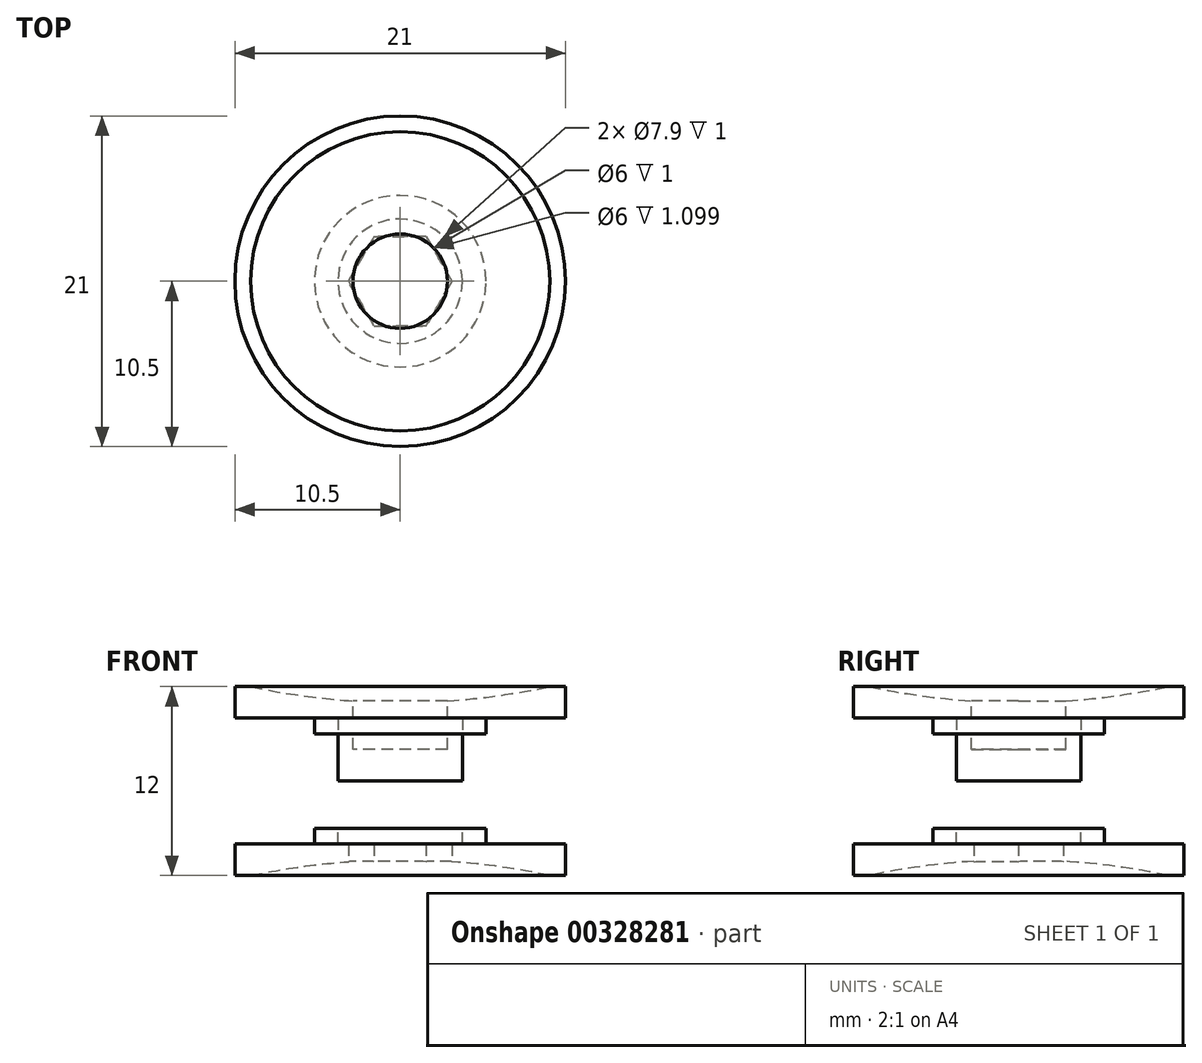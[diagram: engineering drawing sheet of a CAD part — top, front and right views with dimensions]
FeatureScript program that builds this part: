
annotation { "Feature Type Name" : "Feature", "Feature Type Description" : "" }
export const myFeature = defineFeature(function(context is Context, id is Id, definition is map)
    precondition{}
    {
        {
            var Q0;
            Q0=qCreatedBy(makeId("Front.planeOp"),FACE);
            var sketch = newSketch(context, id + "F0", { "sketchPlane" : qUnion([Q0])});
            skLineSegment(sketch, "E0.bottom", {"start": v(0, 15) * mm, "end": v(-3.95, 15) * mm});
            skLineSegment(sketch, "E0.top", {"start": v(0, 19) * mm, "end": v(-3.95, 19) * mm});
            skLineSegment(sketch, "E0.left", {"start": v(0, 15) * mm, "end": v(0, 19) * mm});
            skLineSegment(sketch, "E0.right", {"start": v(-3.95, 15) * mm, "end": v(-3.95, 19) * mm});
            skLineSegment(sketch, "E1.bottom", {"start": v(0, 19) * mm, "end": v(-10.5, 19) * mm});
            skLineSegment(sketch, "E1.top", {"start": v(0, 21) * mm, "end": v(-10.5, 21) * mm});
            skLineSegment(sketch, "E1.left", {"start": v(0, 19) * mm, "end": v(0, 21) * mm});
            skLineSegment(sketch, "E1.right", {"start": v(-10.5, 19) * mm, "end": v(-10.5, 21) * mm});
            skLineSegment(sketch, "E2.bottom", {"start": v(0, 19) * mm, "end": v(-5.45, 19) * mm});
            skLineSegment(sketch, "E2.top", {"start": v(0, 18) * mm, "end": v(-5.45, 18) * mm});
            skLineSegment(sketch, "E2.left", {"start": v(0, 19) * mm, "end": v(0, 18) * mm});
            skLineSegment(sketch, "E2.right", {"start": v(-5.45, 19) * mm, "end": v(-5.45, 18) * mm});
            skLineSegment(sketch, "E3.bottom", {"start": v(0, 18) * mm, "end": v(-1.63, 18) * mm});
            skLineSegment(sketch, "E3.top", {"start": v(0, 15) * mm, "end": v(-1.63, 15) * mm});
            skLineSegment(sketch, "E3.left", {"start": v(0, 18) * mm, "end": v(0, 15) * mm});
            skLineSegment(sketch, "E3.right", {"start": v(-1.63, 18) * mm, "end": v(-1.63, 15) * mm});
            skArc(sketch, "E4", {"start": v(-9.5, 21) * mm, "mid": v(-4.78, 20.25) * mm, "end": v(0, 20) * mm});
            skLineSegment(sketch, "E5.bottom", {"start": v(-1, 18) * mm, "end": v(1, 18) * mm});
            skLineSegment(sketch, "E5.top", {"start": v(-1, 15) * mm, "end": v(1, 15) * mm});
            skLineSegment(sketch, "E5.left", {"start": v(-1, 18) * mm, "end": v(-1, 15) * mm});
            skLineSegment(sketch, "E5.right", {"start": v(1, 18) * mm, "end": v(1, 15) * mm});
            skPoint(sketch, "E5.middle", {"position": v(0, 16.5) * mm});
            skLineSegment(sketch, "E6", {"start": v(0, 0) * mm, "end": v(0, 15) * mm, "construction": true});
            skSolve(sketch);
        }
        {
            var Q0;
            {var subQ6=sQuery(id+"F0.wireOp",EDGE,"E1.bottom");Q0=makeQuery(id+"F0.imprint","IMPRINT",FACE,{"disambiguationData":[TD([[makeQuery(id+"F0.imprint","IMPRINT",EDGE,{"derivedFrom":subQ6}),-1.0]])]});}
            var Q1;
            {var subQ5=sQuery(id+"F0.wireOp",EDGE,"E2.right");Q1=makeQuery(id+"F0.imprint","IMPRINT",FACE,{"disambiguationData":[TD([[makeQuery(id+"F0.imprint","IMPRINT",EDGE,{"derivedFrom":subQ5}),1.0]])]});}
            var Q2;
            {var subQ0=sQuery(id+"F0.wireOp",EDGE,"E2.left");Q2=makeQuery(id+"F0.imprint","IMPRINT",FACE,{"disambiguationData":[TD([[makeQuery(id+"F0.imprint","IMPRINT",EDGE,{"derivedFrom":subQ0}),-1.0]])]});}
            var Q3;
            {var subQ0=sQuery(id+"F0.wireOp",EDGE,"E0.bottom");Q3=makeQuery(id+"F0.imprint","IMPRINT",FACE,{"disambiguationData":[TD([[makeQuery(id+"F0.imprint","IMPRINT",EDGE,{"derivedFrom":subQ0}),-1.0]])]});}
            var Q4;
            Q4=sQuery(id+"F0.wireOp",EDGE,"E0.left");
            revolve(context, id + "F1", {"entities" : qUnion([Q0, Q1, Q2, Q3]), "axis" : qUnion([Q4]), "revolveType" : RevolveType.FULL, "surfaceOperationType" : NewSurfaceOperationType.NEW});
        }
        {
            var Q0;
            Q0=makeQuery(id+"F1.opRevolve","SWEPT_BODY",BODY,{"disambiguationData":[OSD([sQuery(id+"F0.wireOp",EDGE,"E0.bottom"),sQuery(id+"F0.wireOp",EDGE,"E0.right"),sQuery(id+"F0.wireOp",EDGE,"E1.bottom"),sQuery(id+"F0.wireOp",EDGE,"E1.top"),sQuery(id+"F0.wireOp",EDGE,"E1.left"),sQuery(id+"F0.wireOp",EDGE,"E1.right"),sQuery(id+"F0.wireOp",EDGE,"E2.top"),sQuery(id+"F0.wireOp",EDGE,"E2.left"),sQuery(id+"F0.wireOp",EDGE,"E2.right"),sQuery(id+"F0.wireOp",EDGE,"E3.bottom"),sQuery(id+"F0.wireOp",EDGE,"E3.right"),sQuery(id+"F0.wireOp",EDGE,"E4"),sQuery(id+"F0.wireOp",EDGE,"E5.bottom")])]});
            var Q1;
            Q1=makeQuery(id+"F1.opRevolve","SWEPT_FACE",FACE,{"disambiguationData":[OSD([sQuery(id+"F0.wireOp",EDGE,"E0.bottom")])]});
            mirror(context, id + "F2", {"entities" : qUnion([Q0]), "mirrorPlane" : qUnion([Q1])});
        }
        {
            var Q0;
            Q0=makeQuery(id+"F1.opRevolve","SWEPT_FACE",FACE,{"disambiguationData":[OSD([sQuery(id+"F0.wireOp",EDGE,"E1.top")])]});
            var sketch = newSketch(context, id + "F3", { "sketchPlane" : qUnion([Q0])});
            skCircle(sketch, "E7", {"center": v(0, 0) * mm, "radius": 3 * mm});
            skSolve(sketch);
        }
        {
            var Q0;
            Q0=makeQuery(id+"F3.imprint","IMPRINT",FACE,{"disambiguationData":[TD([[makeQuery(id+"F3.imprint","IMPRINT",EDGE,{"derivedFrom":sQuery(id+"F3.wireOp",EDGE,"E7")}),1.0]])]});
            extrude(context, id + "F4", {"entities" : qUnion([Q0]), "operationType" : NewBodyOperationType.REMOVE, "oppositeDirection" : true, "depth" : 4 * mm, "offsetDistance" : 25 * mm});
        }
        {
            var Q0;
            Q0=makeQuery(id+"F2.opPattern","COPY",FACE,{"derivedFrom":makeQuery(id+"F1.opRevolve","SWEPT_FACE",FACE,{"disambiguationData":[OSD([sQuery(id+"F0.wireOp",EDGE,"E1.top")])]}),"instanceName":"1"});
            var sketch = newSketch(context, id + "F5", { "sketchPlane" : qUnion([Q0])});
            skCircle(sketch, "E8.cCircle", {"center": v(0, 0) * mm, "radius": 2.85 * mm, "construction": true});
            skLineSegment(sketch, "E8.0", {"start": v(-1.65, 2.85) * mm, "end": v(1.65, 2.85) * mm});
            skLineSegment(sketch, "E8.1", {"start": v(1.65, 2.85) * mm, "end": v(3.3, 0) * mm});
            skLineSegment(sketch, "E8.2", {"start": v(3.3, 0) * mm, "end": v(1.65, -2.85) * mm});
            skLineSegment(sketch, "E8.3", {"start": v(1.65, -2.85) * mm, "end": v(-1.65, -2.85) * mm});
            skLineSegment(sketch, "E8.4", {"start": v(-1.65, -2.85) * mm, "end": v(-3.3, 0) * mm});
            skLineSegment(sketch, "E8.5", {"start": v(-3.3, 0) * mm, "end": v(-1.65, 2.85) * mm});
            skPoint(sketch, "E8.0.midPoint", {"position": v(0, 2.85) * mm});
            skSolve(sketch);
        }
        {
            var Q0;
            Q0=makeQuery(id+"F5.imprint","IMPRINT",FACE,{"disambiguationData":[TD([[makeQuery(id+"F5.imprint","IMPRINT",EDGE,{"derivedFrom":sQuery(id+"F5.wireOp",EDGE,"E8.0")}),-1.0]])]});
            extrude(context, id + "F6", {"entities" : qUnion([Q0]), "operationType" : NewBodyOperationType.REMOVE, "oppositeDirection" : true, "depth" : 4 * mm, "offsetDistance" : 25 * mm});
        }
    });
